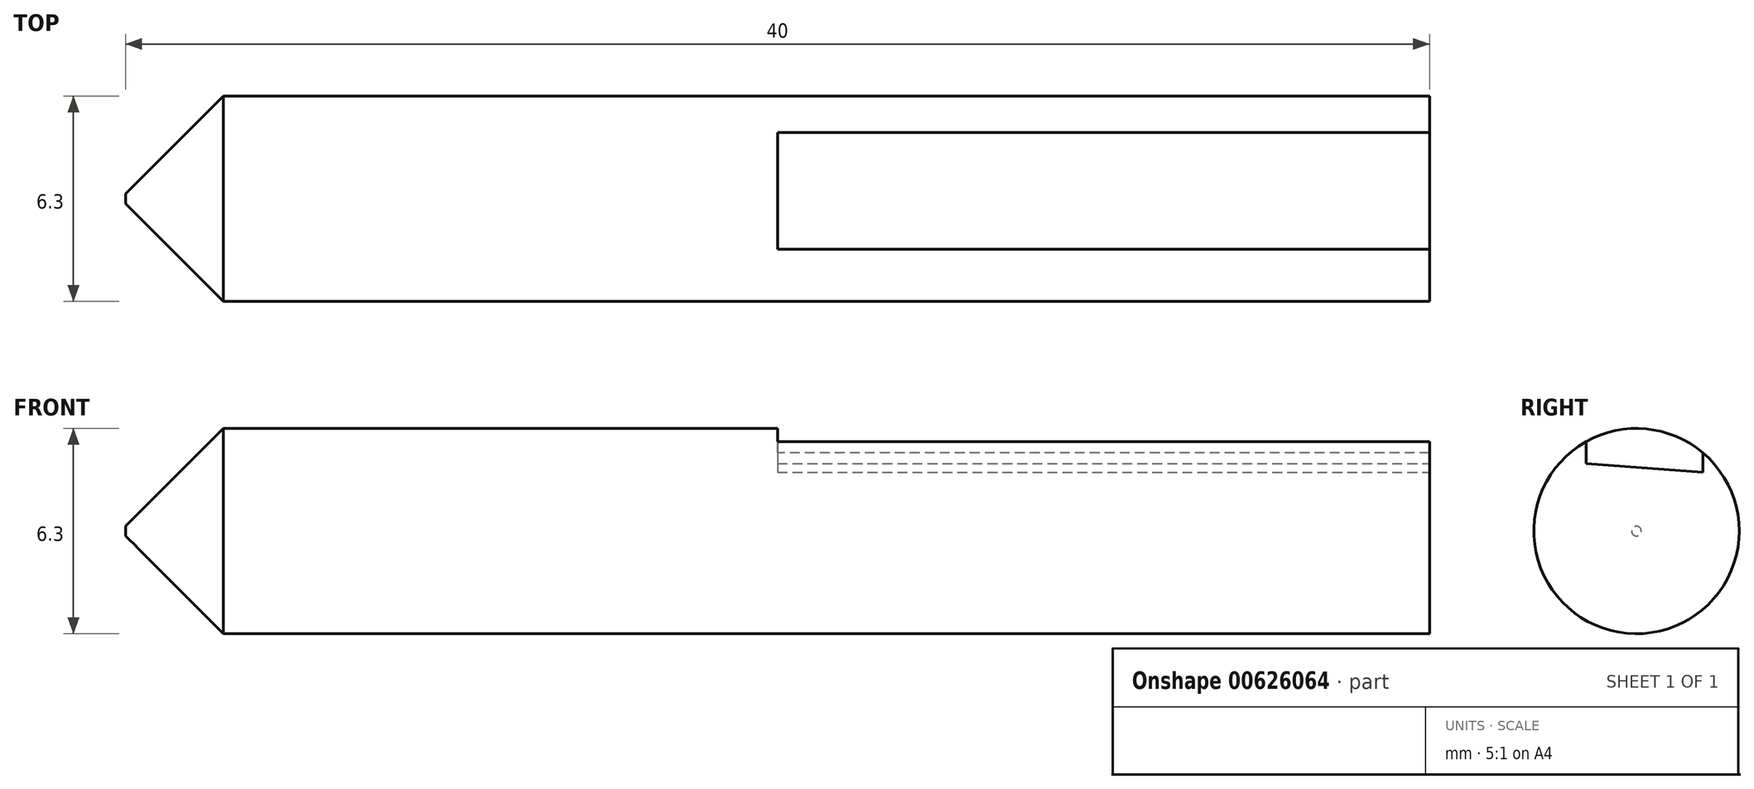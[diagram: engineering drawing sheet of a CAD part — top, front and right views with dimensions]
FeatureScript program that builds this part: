
annotation { "Feature Type Name" : "Feature", "Feature Type Description" : "" }
export const myFeature = defineFeature(function(context is Context, id is Id, definition is map)
    precondition{}
    {
        {
            var Q0;
            Q0=qCreatedBy(makeId("Front.planeOp"),FACE);
            var sketch = newSketch(context, id + "F0", { "sketchPlane" : qUnion([Q0])});
            skLineSegment(sketch, "E0", {"start": v(0, 0) * mm, "end": v(0, 3.15) * mm});
            skLineSegment(sketch, "E1", {"start": v(0, 3.15) * mm, "end": v(40, 3.15) * mm});
            skLineSegment(sketch, "E2", {"start": v(40, 3.15) * mm, "end": v(40, 0) * mm});
            skLineSegment(sketch, "E3", {"start": v(40, 0) * mm, "end": v(0, 0) * mm});
            skSolve(sketch);
        }
        {
            var Q0;
            Q0=makeQuery(id+"F0.imprint","IMPRINT",FACE,{"disambiguationData":[TD([[makeQuery(id+"F0.imprint","IMPRINT",EDGE,{"derivedFrom":sQuery(id+"F0.wireOp",EDGE,"E0")}),-1.0]])]});
            var Q1;
            Q1=sQuery(id+"F0.wireOp",EDGE,"E1");
            revolve(context, id + "F1", {"entities" : qUnion([Q0]), "axis" : qUnion([Q1]), "revolveType" : RevolveType.FULL});
        }
        {
            var Q0;
            Q0=makeQuery(id+"F1.opRevolve","SWEPT_EDGE",EDGE,{"disambiguationData":[OSD([sQuery(id+"F0.wireOp",EDGE,"E0"),sQuery(id+"F0.wireOp",EDGE,"E3")])]});
            chamfer(context, id + "F2", {"entities" : qUnion([Q0]), "width" : 3 * mm, "tangentPropagation" : true});
        }
        {
            var Q0;
            Q0=makeQuery(id+"F1.opRevolve","SWEPT_FACE",FACE,{"disambiguationData":[OSD([sQuery(id+"F0.wireOp",EDGE,"E2")])]});
            var sketch = newSketch(context, id + "F3", { "sketchPlane" : qUnion([Q0])});
            skLineSegment(sketch, "E4", {"start": v(-1.55, 6.88) * mm, "end": v(2.03, 6.62) * mm});
            skLineSegment(sketch, "E5", {"start": v(2.03, 6.62) * mm, "end": v(2.03, 4.96) * mm});
            skLineSegment(sketch, "E6", {"start": v(-1.55, 6.88) * mm, "end": v(-1.55, 5.22) * mm});
            skLineSegment(sketch, "E7", {"start": v(-1.55, 5.22) * mm, "end": v(2.03, 4.96) * mm});
            skSolve(sketch);
        }
        {
            var Q0;
            Q0 = qSketchRegion(id + "F3", true);
            extrude(context, id + "F4", {"entities" : qUnion([Q0]), "operationType" : NewBodyOperationType.REMOVE, "oppositeDirection" : true, "depth" : 20 * mm, "offsetDistance" : 25 * mm});
        }
    });
